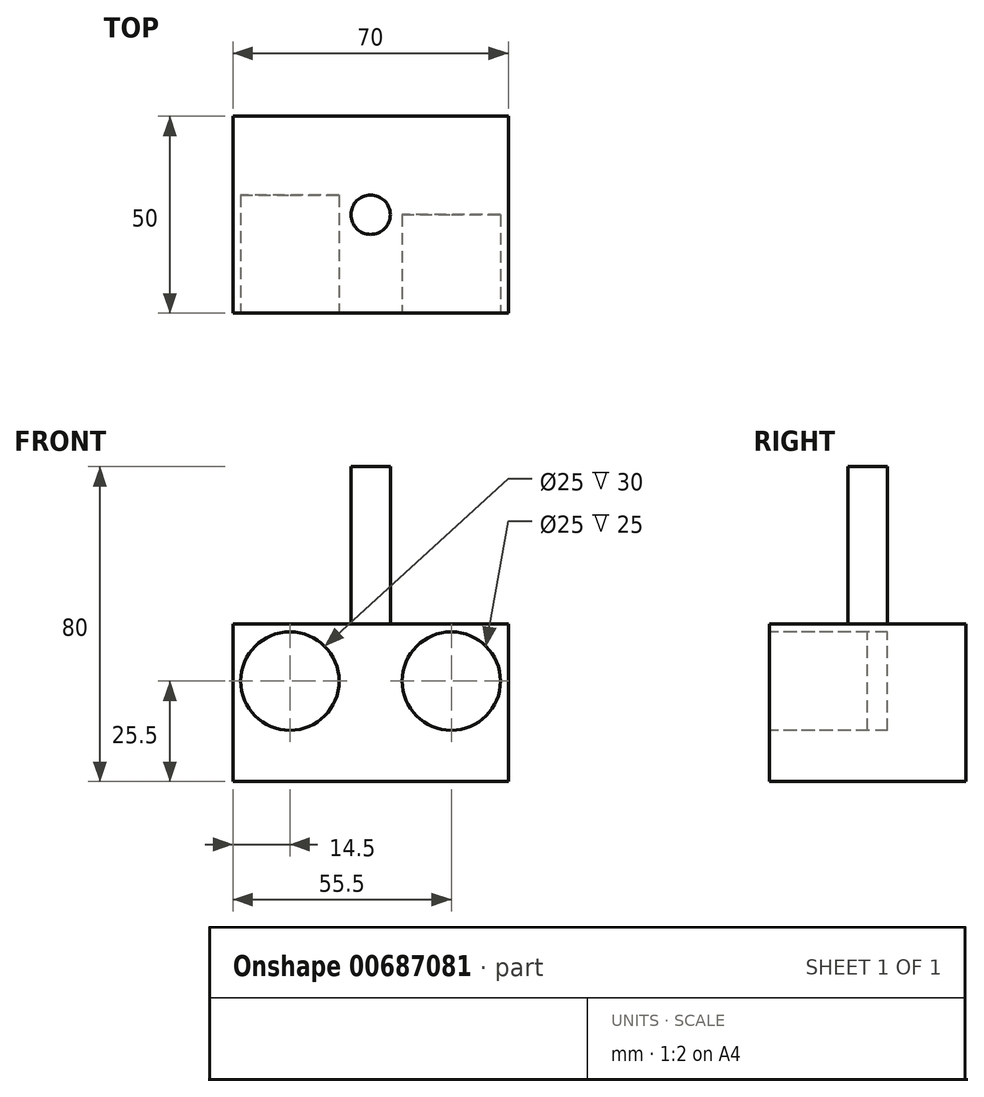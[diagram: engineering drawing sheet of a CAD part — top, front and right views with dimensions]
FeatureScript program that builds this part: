
annotation { "Feature Type Name" : "Feature", "Feature Type Description" : "" }
export const myFeature = defineFeature(function(context is Context, id is Id, definition is map)
    precondition{}
    {
        {
            var Q0;
            Q0=qCreatedBy(makeId("Top.planeOp"),FACE);
            var sketch = newSketch(context, id + "F0", { "sketchPlane" : qUnion([Q0])});
            skLineSegment(sketch, "E0.bottom", {"start": v(-35, -25) * mm, "end": v(35, -25) * mm});
            skLineSegment(sketch, "E0.top", {"start": v(-35, 25) * mm, "end": v(35, 25) * mm});
            skLineSegment(sketch, "E0.left", {"start": v(-35, -25) * mm, "end": v(-35, 25) * mm});
            skLineSegment(sketch, "E0.right", {"start": v(35, -25) * mm, "end": v(35, 25) * mm});
            skPoint(sketch, "E0.middle", {"position": v(0, 0) * mm});
            skSolve(sketch);
        }
        {
            var Q0;
            Q0 = qSketchRegion(id + "F0", true);
            extrude(context, id + "F1", {"entities" : qUnion([Q0]), "depth" : 40 * mm, "offsetDistance" : 25 * mm});
        }
        {
            var Q0;
            Q0=makeQuery(id+"F1.opExtrude","CAP_FACE",FACE,{"disambiguationData":[OSD([sQuery(id+"F0.wireOp",EDGE,"E0.bottom"),sQuery(id+"F0.wireOp",EDGE,"E0.top"),sQuery(id+"F0.wireOp",EDGE,"E0.left"),sQuery(id+"F0.wireOp",EDGE,"E0.right")])],"isStart":false});
            var sketch = newSketch(context, id + "F2", { "sketchPlane" : qUnion([Q0])});
            skCircle(sketch, "E1", {"center": v(0, 0) * mm, "radius": 5 * mm});
            skSolve(sketch);
        }
        {
            var Q0;
            Q0 = qSketchRegion(id + "F2", true);
            extrude(context, id + "F3", {"entities" : qUnion([Q0]), "operationType" : NewBodyOperationType.ADD, "depth" : 40 * mm, "offsetDistance" : 25 * mm});
        }
        {
            var Q0;
            Q0=makeQuery(id+"F1.opExtrude","SWEPT_FACE",FACE,{"disambiguationData":[OSD([sQuery(id+"F0.wireOp",EDGE,"E0.bottom")])]});
            var sketch = newSketch(context, id + "F4", { "sketchPlane" : qUnion([Q0])});
            skCircle(sketch, "E2", {"center": v(-20.5, 25.5) * mm, "radius": 12.5 * mm});
            skSolve(sketch);
        }
        {
            var Q0;
            Q0 = qSketchRegion(id + "F4", true);
            extrude(context, id + "F5", {"entities" : qUnion([Q0]), "operationType" : NewBodyOperationType.REMOVE, "oppositeDirection" : true, "depth" : 30 * mm, "offsetDistance" : 25 * mm});
        }
        {
            var Q0;
            Q0=makeQuery(id+"F1.opExtrude","SWEPT_FACE",FACE,{"disambiguationData":[OSD([sQuery(id+"F0.wireOp",EDGE,"E0.bottom")])]});
            var sketch = newSketch(context, id + "F6", { "sketchPlane" : qUnion([Q0])});
            skCircle(sketch, "E3", {"center": v(20.5, 25.5) * mm, "radius": 12.5 * mm});
            skSolve(sketch);
        }
        {
            var Q0;
            Q0 = qSketchRegion(id + "F6", true);
            extrude(context, id + "F7", {"entities" : qUnion([Q0]), "operationType" : NewBodyOperationType.REMOVE, "oppositeDirection" : true, "depth" : 25 * mm, "offsetDistance" : 25 * mm});
        }
    });
